# Revit family: DFM Doors - double leaf door EI 60
name_source: partatom
category: Doors
revit_build: Autodesk Revit 2017 (Build: 20190507_1515(x64)
units: mm (PartAtom-declared; Revit-internal decimal feet)

## family parameters
Always vertical = Yes
Cut with Voids When Loaded = No
Host = Wall
OmniClass Number = 23.30.10.00
OmniClass Title = Doors
Room Calculation Point = Yes
Shared = No

## types (1)
- 2018x1840 internal frame
    Clear opening height = 2018 mm  [stored 6.62073 ft]
    Clear opening height. Limiting dimensions = ok
    Clear opening width = 1840 mm  [stored 6.03675 ft]
    Clear opening width at opened active leaf = 900 mm  [stored 2.95276 ft]
    Clear opening width. Limiting dimensions = ok
    Corner frame = No
    Embracing frame = No
    Fire Rating = EI 60
    Frame to frame width = 1896 mm  [stored 6.22047 ft]
    Function = Interior
    Height = 2085 mm  [stored 6.84055 ft]
    Height of the door leaf = 2037 mm  [stored 6.68307 ft]
    Internal frame = Yes
    Manufacturer = DFM Doors sp. z o. o.
    Material of astragal profie = DFM Doors - aluminium
    Material of cut-off for the ventilation grid KWZ = DFM Doors - cut-off for the ventilation grid 1
    Material of cut-off for the ventilation grid NV and ZET = DFM Doors - cut-off for the ventilation grid 2
    Material of door closer = DFM Doors - aluminium
    Material of door frame = DFM Doors - aluminium
    Material of door leaf = DFM Doors - zinc coated steel
    Material of drip cap = DFM Doors - zinc coated steel
    Material of glass = DFM Doors - glazing
    Material of glass framing = DFM Doors - zinc coated steel
    Material of hinges = DFM Doors - stainless steel
    Material of ironmongery = DFM Doors - aluminium
    Material of ventilation grid = DFM Doors - zinc coated steel
    Model = DFM DS 60 - 2
    Offset of the active leaf axis = 524 mm  [stored 1.71916 ft]
    Offset of the door leaf = 59 mm
    Offset of the inter-leaf axis = 1015 mm  [stored 3.33005 ft]
    Offset of the passive leaf axis = 524 mm  [stored 1.71916 ft]
    Rough Height = 2085 mm  [stored 6.84055 ft]
    Rough Width = 2030 mm  [stored 6.6601 ft]
    Thickness = 65 mm  [stored 0.213255 ft]
    Type of frame = 2
    URL = https://www.dfm-europe.eu
    Wall Closure = By host
    Width = 2030 mm  [stored 6.6601 ft]
    Width of active leaf = 974 mm  [stored 3.19554 ft]
    Width of active leaf. Limiting dimensions = ok
    Width of passive leaf = 974 mm  [stored 3.19554 ft]
    Width of passive leaf. Limiting dimensions = ok

note: [stored X ft] marks values corroborated as IEEE doubles in the binary element streams (Revit-internal decimal feet)
